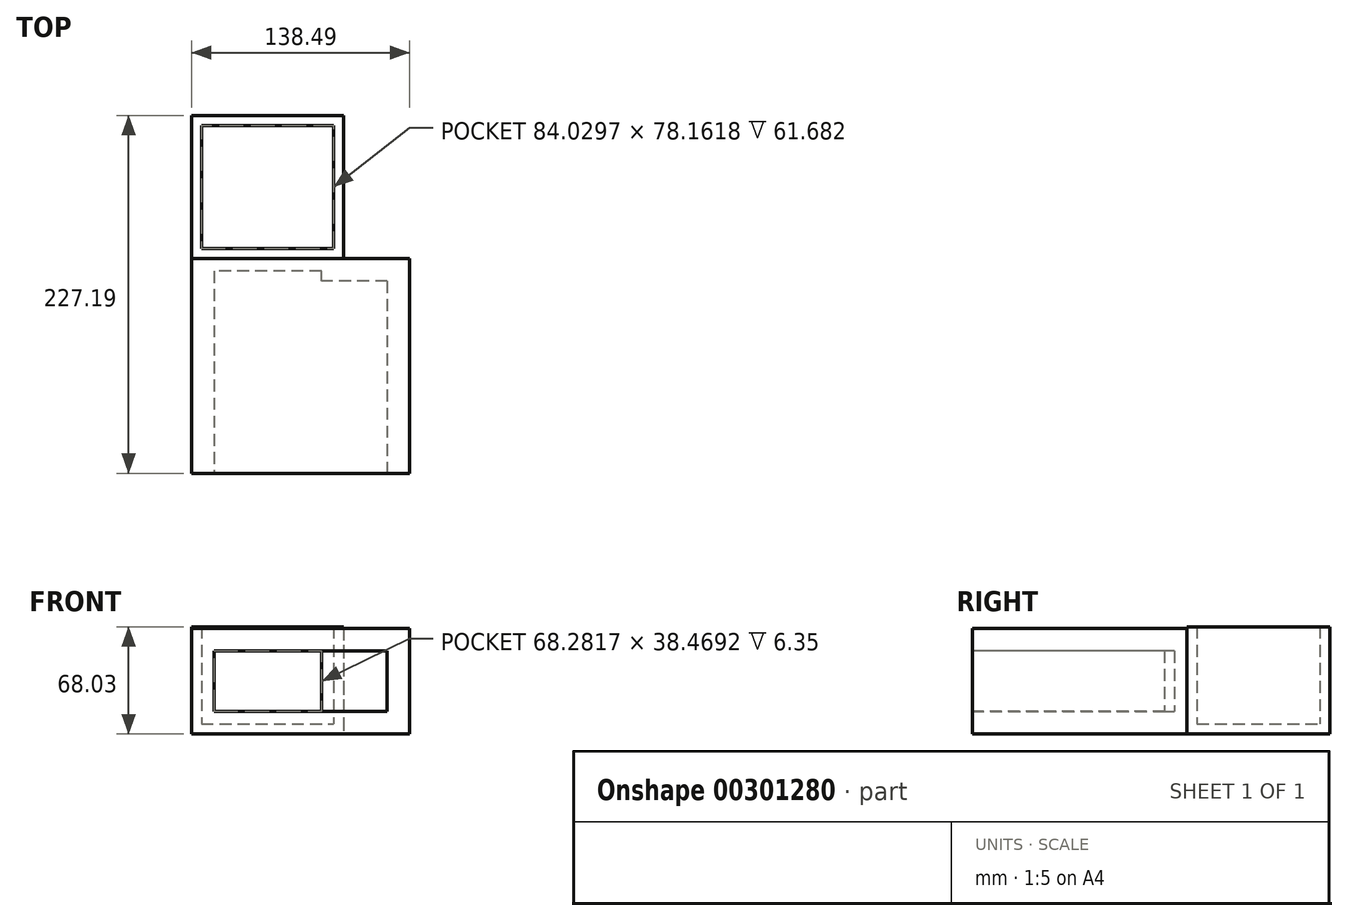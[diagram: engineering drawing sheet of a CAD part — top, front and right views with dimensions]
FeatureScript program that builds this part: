
annotation { "Feature Type Name" : "Feature", "Feature Type Description" : "" }
export const myFeature = defineFeature(function(context is Context, id is Id, definition is map)
    precondition{}
    {
        {
            var Q0;
            Q0=qCreatedBy(makeId("Top.planeOp"),FACE);
            var sketch = newSketch(context, id + "F0", { "sketchPlane" : qUnion([Q0])});
            skLineSegment(sketch, "E0.bottom", {"start": v(0, 0) * mm, "end": v(96.73, 0) * mm});
            skLineSegment(sketch, "E0.top", {"start": v(0, 90.86) * mm, "end": v(96.73, 90.86) * mm});
            skLineSegment(sketch, "E0.left", {"start": v(0, 0) * mm, "end": v(0, 90.86) * mm});
            skLineSegment(sketch, "E0.right", {"start": v(96.73, 0) * mm, "end": v(96.73, 90.86) * mm});
            skSolve(sketch);
        }
        {
            var Q0;
            Q0 = qSketchRegion(id + "F0", true);
            extrude(context, id + "F1", {"entities" : qUnion([Q0]), "depth" : 68.03 * mm});
        }
        {
            var Q0;
            Q0=makeQuery(id+"F1.opExtrude","CAP_FACE",FACE,{"disambiguationData":[OSD([sQuery(id+"F0.wireOp",EDGE,"E0.bottom"),sQuery(id+"F0.wireOp",EDGE,"E0.top"),sQuery(id+"F0.wireOp",EDGE,"E0.left"),sQuery(id+"F0.wireOp",EDGE,"E0.right")])],"isStart":false});
            shell(context, id + "F2", {"entities" : qUnion([Q0]), "thickness" : 6.35 * mm});
        }
        {
            var Q0;
            Q0=qCreatedBy(makeId("Right.planeOp"),FACE);
            var sketch = newSketch(context, id + "F3", { "sketchPlane" : qUnion([Q0])});
            skLineSegment(sketch, "E1.bottom", {"start": v(0, 0) * mm, "end": v(-136.33, 0) * mm});
            skLineSegment(sketch, "E1.top", {"start": v(0, 66.92) * mm, "end": v(-136.33, 66.92) * mm});
            skLineSegment(sketch, "E1.left", {"start": v(0, 0) * mm, "end": v(0, 66.92) * mm});
            skLineSegment(sketch, "E1.right", {"start": v(-136.33, 0) * mm, "end": v(-136.33, 66.92) * mm});
            skSolve(sketch);
        }
        {
            var Q0;
            Q0=makeQuery(id+"F3.imprint","IMPRINT",FACE,{"disambiguationData":[TD([[makeQuery(id+"F3.imprint","IMPRINT",EDGE,{"derivedFrom":sQuery(id+"F3.wireOp",EDGE,"E1.bottom")}),-1.0]])]});
            extrude(context, id + "F4", {"entities" : qUnion([Q0]), "operationType" : NewBodyOperationType.ADD, "depth" : 138.5 * mm});
        }
        {
            var Q0;
            Q0=makeQuery(id+"F4.opExtrude","SWEPT_FACE",FACE,{"disambiguationData":[OSD([sQuery(id+"F3.wireOp",EDGE,"E1.right")])]});
            shell(context, id + "F5", {"entities" : qUnion([Q0]), "thickness" : 14.22 * mm});
        }
    });
